FCSTD DOCUMENT  (FreeCAD 0.20R29177 (Git))
Label: Cote10PortraitVesa
License: All rights reserved
LicenseURL: http://en.wikipedia.org/wiki/All_rights_reserved
objects: TechDraw::DrawViewDimension×36, TechDraw::DrawSVGTemplate×2, TechDraw::DrawPage×2, Sketcher::SketchObject×1, PartDesign::Body×1, TechDraw::DrawProjGroupItem×1, TechDraw::DrawProjGroup×1
note: 2 computed .brp shape members not serialized (recipe doc carries the construction recipe); baked Part::Feature solids carry a one-line shape summary decoded from their .brp
EXTERNAL_REF file=DonneesBoitier.FCStd obj=Spreadsheet

FEATURE [Sketcher::SketchObject] Sketch
  FullyConstrained = true
  MapMode = 5
  Support = -> [XY_Plane001]
  expr: Constraints[0] = <<DonneesBoitier>>#<<Spreadsheet>>.xxHauteur - <<DonneesBoitier>>#<<Spreadsheet>>.xxFaEspaceHaut / 2 + <<DonneesBoitier>>#<<Spreadsheet>>.xxHautEncocheFemelle / 2
  expr: Constraints[106] = 10mm
  expr: Constraints[108] = 10mm
  expr: Constraints[109] = 15mm
  expr: Constraints[112] = 15mm
  expr: Constraints[117] = <<DonneesBoitier>>#<<Spreadsheet>>.xxDistEcrou
  expr: Constraints[147] = <<DonneesBoitier>>#<<Spreadsheet>>.xxLongVis
  expr: Constraints[148] = <<DonneesBoitier>>#<<Spreadsheet>>.xxLongVis
  expr: Constraints[151] = <<DonneesBoitier>>#<<Spreadsheet>>.xxEspaceTrouEncoche * 2
  expr: Constraints[158] = <<DonneesBoitier>>#<<Spreadsheet>>.xxEpaisseurEcran - <<DonneesBoitier>>#<<Spreadsheet>>.xxEpEncoche
  expr: Constraints[24] = <<DonneesBoitier>>#<<Spreadsheet>>.xxLongEncoches
  expr: Constraints[262] = <<DonneesBoitier>>#<<Spreadsheet>>.xxDiametreTrou
  expr: Constraints[297] = <<DonneesBoitier>>#<<Spreadsheet>>.xxEspaceTrouEncoche
  expr: Constraints[299] = <<DonneesBoitier>>#<<Spreadsheet>>.xxHauteur - <<DonneesBoitier>>#<<Spreadsheet>>.xxHauteurEncasEcran - <<DonneesBoitier>>#<<Spreadsheet>>.xxFaEspaceHaut * 1.5
  expr: Constraints[36] = <<DonneesBoitier>>#<<Spreadsheet>>.xxLargEconche
  expr: Constraints[59] = <<DonneesBoitier>>#Spreadsheet.xxLargLatHaut
  expr: Constraints[60] = 25mm
  expr: Constraints[61] = <<DonneesBoitier>>#Spreadsheet.xxHauteurEncasEcran / 2 + <<DonneesBoitier>>#Spreadsheet.xxHautEncocheFemelle / 2 + <<DonneesBoitier>>#Spreadsheet.xxFaEspaceHaut / 2
  expr: Constraints[96] = <<DonneesBoitier>>#<<Spreadsheet>>.xxEpEcrou
  sketch-geometry (110):
    g0: LineSegment StartX=0 StartY=0 StartZ=0 EndX=-195.5 EndY=0 EndZ=0
    g1: LineSegment StartX=0 StartY=0 StartZ=0 EndX=6e-16 EndY=10 EndZ=0
    g2: LineSegment StartX=6e-16 StartY=10 StartZ=0 EndX=-8.66025 EndY=15 EndZ=0
    g3: LineSegment StartX=-8.66025 StartY=15 StartZ=0 EndX=-8.66025 EndY=10 EndZ=0
    g4: ArcOfCircle CenterX=0 CenterY=76.1243 CenterZ=0 NormalX=0 NormalY=0 NormalZ=1 AngleXU=0 Radius=66.689 StartAngle=2.73334 EndAngle=4.58216
    g5: LineSegment StartX=-34.7885 StartY=158.361 StartZ=0 EndX=-38.2526 EndY=160.361 EndZ=0
    g6: LineSegment StartX=-42.2526 StartY=153.432 StartZ=0 EndX=-38.7885 EndY=151.432 EndZ=0
    g7: LineSegment StartX=-42.2526 StartY=153.432 StartZ=0 EndX=-41.5651 EndY=154.623 EndZ=0
    g8: LineSegment StartX=-41.5651 StartY=154.623 StartZ=0 EndX=-44.1632 EndY=156.123 EndZ=0
    g9: LineSegment StartX=-44.1632 StartY=156.123 StartZ=0 EndX=-41.5382 EndY=160.67 EndZ=0
    g10: LineSegment StartX=-41.5382 StartY=160.67 StartZ=0 EndX=-38.9401 EndY=159.17 EndZ=0
    g11: LineSegment StartX=-38.9401 StartY=159.17 StartZ=0 EndX=-38.2526 EndY=160.361 EndZ=0
    g12: LineSegment StartX=-83.2859 StartY=186.361 StartZ=0 EndX=-79.8218 EndY=184.361 EndZ=0
    g13: LineSegment StartX=-83.8218 StartY=177.432 StartZ=0 EndX=-87.2859 EndY=179.432 EndZ=0
    g14: LineSegment StartX=-83.8218 StartY=177.432 StartZ=0 EndX=-83.1343 EndY=178.623 EndZ=0
    g15: LineSegment StartX=-83.1343 StartY=178.623 StartZ=0 EndX=-79.6702 EndY=176.623 EndZ=0
    g16: LineSegment StartX=-79.6702 StartY=176.623 StartZ=0 EndX=-77.0452 EndY=181.17 EndZ=0
    g17: LineSegment StartX=-77.0452 StartY=181.17 StartZ=0 EndX=-80.5093 EndY=183.17 EndZ=0
    g18: LineSegment StartX=-80.5093 StartY=183.17 StartZ=0 EndX=-79.8218 EndY=184.361 EndZ=0
    g19: LineSegment StartX=-12.95 StartY=316.186 StartZ=0 EndX=8.70064 EndY=303.686 EndZ=0
    g20: LineSegment StartX=21.691 StartY=296.186 StartZ=0 EndX=43.3417 EndY=283.686 EndZ=0
    g21: LineSegment StartX=8.70064 StartY=303.686 StartZ=0 EndX=6.20064 EndY=299.356 EndZ=0
    g22: LineSegment StartX=6.20064 StartY=299.356 StartZ=0 EndX=19.191 EndY=291.856 EndZ=0
    g23: LineSegment StartX=19.191 StartY=291.856 StartZ=0 EndX=21.691 EndY=296.186 EndZ=0
    g24: LineSegment StartX=-32.4583 StartY=152.396 StartZ=0 EndX=-88.75 EndY=184.896 EndZ=0
    g25: LineSegment StartX=-43.7083 StartY=132.911 StartZ=0 EndX=-100 EndY=165.411 EndZ=0
    g26: LineSegment StartX=43.3417 StartY=283.686 StartZ=0 EndX=-17.4583 EndY=178.377 EndZ=0
    g27: LineSegment StartX=-47.4583 StartY=126.416 StartZ=0 EndX=-61.2083 EndY=102.6 EndZ=0
    g28: LineSegment StartX=-17.4583 StartY=178.377 StartZ=0 EndX=-13.1282 EndY=175.877 EndZ=0
    g29: LineSegment StartX=-13.1282 StartY=175.877 StartZ=0 EndX=-20.6282 EndY=162.887 EndZ=0
    g30: LineSegment StartX=-20.6282 StartY=162.887 StartZ=0 EndX=-24.9583 EndY=165.387 EndZ=0
    g31: LineSegment StartX=-39.9583 StartY=139.406 StartZ=0 EndX=-35.6282 EndY=136.906 EndZ=0
    g32: LineSegment StartX=-35.6282 StartY=136.906 StartZ=0 EndX=-43.1282 EndY=123.916 EndZ=0
    g33: LineSegment StartX=-43.1282 StartY=123.916 StartZ=0 EndX=-47.4583 EndY=126.416 EndZ=0
    g34: LineSegment StartX=-81.25 StartY=197.887 StartZ=0 EndX=-85.5801 EndY=200.387 EndZ=0
    g35: LineSegment StartX=-85.5801 StartY=200.387 StartZ=0 EndX=-78.0801 EndY=213.377 EndZ=0
    g36: LineSegment StartX=-78.0801 StartY=213.377 StartZ=0 EndX=-73.75 EndY=210.877 EndZ=0
    g37: LineSegment StartX=-103.75 StartY=158.916 StartZ=0 EndX=-108.08 EndY=161.416 EndZ=0
    g38: LineSegment StartX=-108.08 StartY=161.416 StartZ=0 EndX=-100.58 EndY=174.406 EndZ=0
    g39: LineSegment StartX=-100.58 StartY=174.406 StartZ=0 EndX=-96.25 EndY=171.906 EndZ=0
    g40: LineSegment StartX=-195.5 StartY=0 StartZ=0 EndX=5.68e-14 EndY=338.616 EndZ=0
    g41: LineSegment StartX=-35.476 StartY=157.17 StartZ=0 EndX=-34.7885 EndY=158.361 EndZ=0
    g42: LineSegment StartX=-38.7885 StartY=151.432 StartZ=0 EndX=-38.101 EndY=152.623 EndZ=0
    g43: LineSegment StartX=-24.9583 StartY=165.387 StartZ=0 EndX=-31.1458 EndY=154.67 EndZ=0
    g44: LineSegment StartX=-33.7708 StartY=150.123 StartZ=0 EndX=-39.9583 EndY=139.406 EndZ=0
    g45: LineSegment StartX=-35.476 StartY=157.17 StartZ=0 EndX=-31.1458 EndY=154.67 EndZ=0
    g46: LineSegment StartX=-38.101 StartY=152.623 StartZ=0 EndX=-33.7708 EndY=150.123 EndZ=0
    g47: LineSegment StartX=-96.25 StartY=171.906 StartZ=0 EndX=-90.0625 EndY=182.623 EndZ=0
    g48: LineSegment StartX=-81.25 StartY=197.887 StartZ=0 EndX=-87.4375 EndY=187.17 EndZ=0
    g49: LineSegment StartX=-83.9734 StartY=185.17 StartZ=0 EndX=-83.2859 EndY=186.361 EndZ=0
    g50: LineSegment StartX=-87.2859 StartY=179.432 StartZ=0 EndX=-86.5984 EndY=180.623 EndZ=0
    g51: LineSegment StartX=-90.0625 StartY=182.623 StartZ=0 EndX=-86.5984 EndY=180.623 EndZ=0
    g52: LineSegment StartX=-87.4375 StartY=187.17 StartZ=0 EndX=-83.9734 EndY=185.17 EndZ=0
    g53: LineSegment StartX=-73.75 StartY=210.877 StartZ=0 EndX=-58.75 EndY=236.858 EndZ=0
    g54: LineSegment StartX=-58.75 StartY=236.858 StartZ=0 EndX=-12.95 EndY=316.186 EndZ=0
    g55: LineSegment StartX=-118.75 StartY=132.935 StartZ=0 EndX=-103.75 EndY=158.916 EndZ=0
    g56: LineSegment StartX=-173.561 StartY=0 StartZ=0 EndX=3.50448 EndY=306.686 EndZ=0
    g57: LineSegment StartX=-12.2955 StartY=279.319 StartZ=0 EndX=-7.96539 EndY=276.819 EndZ=0
    g58: LineSegment StartX=-7.96539 StartY=276.819 StartZ=0 EndX=-15.4654 EndY=263.829 EndZ=0
    g59: LineSegment StartX=-15.4654 StartY=263.829 StartZ=0 EndX=-19.7955 EndY=266.329 EndZ=0
    g60: LineSegment StartX=-19.7955 StartY=266.329 StartZ=0 EndX=-12.2955 EndY=279.319 EndZ=0
    g61: LineSegment StartX=-34.7955 StartY=240.348 StartZ=0 EndX=-30.4654 EndY=237.848 EndZ=0
    g62: LineSegment StartX=-30.4654 StartY=237.848 StartZ=0 EndX=-37.9654 EndY=224.858 EndZ=0
    g63: LineSegment StartX=-42.2955 StartY=227.358 StartZ=0 EndX=-34.7955 EndY=240.348 EndZ=0
    g64: LineSegment StartX=-37.9654 StartY=224.858 StartZ=0 EndX=-42.2955 EndY=227.358 EndZ=0
    g65: LineSegment StartX=-57.2955 StartY=201.377 StartZ=0 EndX=-52.9654 EndY=198.877 EndZ=0
    g66: LineSegment StartX=-52.9654 StartY=198.877 StartZ=0 EndX=-60.4654 EndY=185.887 EndZ=0
    g67: LineSegment StartX=-64.7955 StartY=188.387 StartZ=0 EndX=-57.2955 EndY=201.377 EndZ=0
    g68: LineSegment StartX=-60.4654 StartY=185.887 StartZ=0 EndX=-64.7955 EndY=188.387 EndZ=0
    g69: LineSegment StartX=-85.5801 StartY=200.387 StartZ=0 EndX=-60.4654 EndY=185.887 EndZ=0
    g70: LineSegment StartX=-132.296 StartY=71.4734 StartZ=0 EndX=-127.965 EndY=68.9734 EndZ=0
    g71: LineSegment StartX=-127.965 StartY=68.9734 StartZ=0 EndX=-120.465 EndY=81.9638 EndZ=0
    g72: LineSegment StartX=-120.465 StartY=81.9638 StartZ=0 EndX=-124.796 EndY=84.4638 EndZ=0
    g73: LineSegment StartX=-124.796 StartY=84.4638 StartZ=0 EndX=-132.296 EndY=71.4734 EndZ=0
    g74: LineSegment StartX=-109.796 StartY=110.445 StartZ=0 EndX=-105.465 EndY=107.945 EndZ=0
    g75: LineSegment StartX=-105.465 StartY=107.945 StartZ=0 EndX=-97.9654 EndY=120.935 EndZ=0
    g76: LineSegment StartX=-102.296 StartY=123.435 StartZ=0 EndX=-109.796 EndY=110.445 EndZ=0
    g77: LineSegment StartX=-97.9654 StartY=120.935 StartZ=0 EndX=-102.296 EndY=123.435 EndZ=0
    g78: LineSegment StartX=-87.2955 StartY=149.416 StartZ=0 EndX=-82.9654 EndY=146.916 EndZ=0
    g79: LineSegment StartX=-82.9654 StartY=146.916 StartZ=0 EndX=-75.4654 EndY=159.906 EndZ=0
    g80: LineSegment StartX=-79.7955 StartY=162.406 StartZ=0 EndX=-87.2955 EndY=149.416 EndZ=0
    g81: LineSegment StartX=-75.4654 StartY=159.906 StartZ=0 EndX=-79.7955 EndY=162.406 EndZ=0
    g82: LineSegment StartX=-195.5 StartY=0 StartZ=0 EndX=-178.25 EndY=29.8779 EndZ=0
    g83: LineSegment StartX=-170.75 StartY=42.8683 StartZ=0 EndX=-164.563 EndY=53.5853 EndZ=0
    g84: LineSegment StartX=-161.938 StartY=58.132 StartZ=0 EndX=-155.75 EndY=68.849 EndZ=0
    g85: LineSegment StartX=-148.25 StartY=81.8394 StartZ=0 EndX=-118.75 EndY=132.935 EndZ=0
    g86: LineSegment StartX=-148.25 StartY=81.8394 StartZ=0 EndX=-152.58 EndY=84.3394 EndZ=0
    g87: LineSegment StartX=-152.58 StartY=84.3394 StartZ=0 EndX=-160.08 EndY=71.349 EndZ=0
    g88: LineSegment StartX=-160.08 StartY=71.349 StartZ=0 EndX=-155.75 EndY=68.849 EndZ=0
    g89: LineSegment StartX=-170.75 StartY=42.8683 StartZ=0 EndX=-175.08 EndY=45.3683 EndZ=0
    g90: LineSegment StartX=-175.08 StartY=45.3683 StartZ=0 EndX=-182.58 EndY=32.3779 EndZ=0
    g91: LineSegment StartX=-182.58 StartY=32.3779 StartZ=0 EndX=-178.25 EndY=29.8779 EndZ=0
    g92: LineSegment StartX=-164.563 StartY=53.5853 StartZ=0 EndX=-161.098 EndY=51.5853 EndZ=0
    g93: LineSegment StartX=-161.098 StartY=51.5853 StartZ=0 EndX=-161.786 EndY=50.3945 EndZ=0
    g94: LineSegment StartX=-161.786 StartY=50.3945 StartZ=0 EndX=-158.322 EndY=48.3945 EndZ=0
    g95: LineSegment StartX=-158.322 StartY=48.3945 StartZ=0 EndX=-157.634 EndY=49.5853 EndZ=0
    g96: LineSegment StartX=-157.634 StartY=49.5853 StartZ=0 EndX=-154.17 EndY=47.5853 EndZ=0
    g97: LineSegment StartX=-154.17 StartY=47.5853 StartZ=0 EndX=-151.545 EndY=52.132 EndZ=0
    g98: LineSegment StartX=-151.545 StartY=52.132 StartZ=0 EndX=-155.009 EndY=54.132 EndZ=0
    g99: LineSegment StartX=-155.009 StartY=54.132 StartZ=0 EndX=-154.322 EndY=55.3227 EndZ=0
    g100: LineSegment StartX=-154.322 StartY=55.3227 StartZ=0 EndX=-157.786 EndY=57.3227 EndZ=0
    g101: LineSegment StartX=-157.786 StartY=57.3227 StartZ=0 EndX=-158.473 EndY=56.132 EndZ=0
    g102: LineSegment StartX=-158.473 StartY=56.132 StartZ=0 EndX=-161.938 EndY=58.132 EndZ=0
    g103: GeomPoint X=-163.25 Y=55.8586 Z=0
    g104: LineSegment StartX=-195.5 StartY=0 StartZ=0 EndX=-162.591 EndY=19 EndZ=0
    g105: ArcOfCircle CenterX=-178.179 CenterY=10 CenterZ=0 NormalX=0 NormalY=0 NormalZ=1 AngleXU=0 Radius=10 StartAngle=2.61799 EndAngle=4.71239
    g106: LineSegment StartX=-12.95 StartY=316.186 StartZ=0 EndX=-5.99552 EndY=290.231 EndZ=0
    g107: LineSegment StartX=43.3417 StartY=283.686 StartZ=0 EndX=-19.4955 EndY=266.849 EndZ=0
    g108: ArcOfCircle CenterX=-7.77362 CenterY=296.867 CenterZ=0 NormalX=0 NormalY=0 NormalZ=1 AngleXU=0 Radius=14.1421 StartAngle=1.0472 EndAngle=2.61799
    g109: ArcOfCircle CenterX=24.0231 CenterY=278.509 CenterZ=0 NormalX=0 NormalY=0 NormalZ=1 AngleXU=0 Radius=14.1421 StartAngle=5.75959 EndAngle=7.33038
  constraints (322):
    c: Distance(g0,g19) = 365.1
    c: Tangent(g19,g20)
    c: Parallel(g26,g29)
    c: Parallel(g29,g35)
    c: Parallel(g32,g38)
    c: Parallel(g21,g23)
    c: Coincident(g19,g54)
    c: Coincident(g21,g19)
    c: Coincident(g23,g20)
    c: Coincident(g20,g26)
    c: Coincident(g53,g36)
    c: Coincident(g35,g34)
    c: Coincident(g26,g28)
    c: Coincident(g29,g28)
    c: Coincident(g29,g30)
    c: Coincident(g30,g43)
    c: Parallel(g36,g19)
    c: Parallel(g34,g19)
    c: Parallel(g28,g30)
    c: Parallel(g30,g20)
    c: Parallel(g37,g39)
    c: Parallel(g39,g31)
    c: Parallel(g31,g33)
    c: Parallel(g33,g20)
    c: Distance(g26,g28) = 5
    c: Equal(g28,g36)
    c: Equal(g36,g34)
    c: Equal(g34,g30)
    c: Equal(g30,g23)
    c: Equal(g23,g21)
    c: Equal(g30,g31)
    c: Equal(g31,g33)
    c: Equal(g33,g37)
    c: Equal(g37,g39)
    c: Coincident(g22,g21)
    c: Coincident(g22,g23)
    c: Distance(g21,g22) = 15
    c: Equal(g22,g35)
    c: Equal(g35,g29)
    c: Equal(g29,g32)
    c: Equal(g32,g38)
    c: Coincident(g35,g36)
    c: PointOnObject(g0,g-1)
    c: Coincident(g55,g37)
    c: Coincident(g38,g39)
    c: Coincident(g37,g38)
    c: Coincident(g40,g0)
    c: PointOnObject(g40,g-2)
    c: Angle(g0,g40) = 1.0472
    c: Distance(g0,g40) = 391
    c: Coincident(g0,g1)
    c: Coincident(g0,g-1)
    c: Symmetric(g39,g55,g25)
    c: Coincident(g44,g31)
    c: Coincident(g32,g31)
    c: Coincident(g32,g33)
    c: Coincident(g27,g33)
    c: Symmetric(g27,g44,g25)
    c: Coincident(g27,g4)
    c: Distance(g19,g20) = 65
    c: Distance(g19,g19) = 25
    c: Distance(g20,g24) = 151.6
    c: Symmetric(g8,g9,g24)
    c: Symmetric(g15,g16,g24)
    c: Coincident(g41,g5)
    c: Coincident(g10,g9)
    c: Coincident(g9,g8)
    c: Coincident(g42,g6)
    c: Parallel(g8,g10)
    c: Parallel(g10,g24)
    c: Coincident(g11,g10)
    c: Parallel(g11,g7)
    c: Parallel(g7,g9)
    c: Coincident(g5,g11)
    c: Parallel(g5,g6)
    c: Parallel(g6,g24)
    c: Coincident(g6,g7)
    c: Coincident(g8,g7)
    c: Distance(g5,g41) = 4
    c: Equal(g5,g6)
    c: Distance(g42,g41) = 8
    c: Symmetric(g41,g42,g24)
    c: Distance(g8,g9) = 5.25
    c: Symmetric(g39,g34,g24)
    c: Coincident(g16,g17)
    c: Coincident(g15,g16)
    c: Coincident(g13,g50)
    c: Coincident(g12,g49)
    c: Symmetric(g14,g17,g24)
    c: Symmetric(g12,g13,g24)
    c: Parallel(g24,g17)
    c: Parallel(g17,g12)
    c: Coincident(g18,g12)
    c: Coincident(g18,g17)
    c: Coincident(g15,g14)
    c: Coincident(g14,g13)
    c: Distance(g49,g12) = 4
    c: Distance(g50,g49) = 8
    c: Distance(g15,g16) = 5.25
    c: Parallel(g13,g24)
    c: PointOnObject(g24,g40)
    c: PointOnObject(g4,g-2)
    c: Coincident(g4,g3)
    c: Coincident(g1,g2)
    c: Coincident(g2,g3)
    c: Distance(g2,g3) = 5
    c: Distance(g2,g1) = 10
    c: Angle(g-1,g1) = 1.5708
    c: Distance(g0,g1) = 10
    c: Distance(g2,g0) = 15
    c: Distance(g4,g27) = 27.5
    c: Parallel(g3,g1)
    c: Distance(g43,g24) = 15
    c: Parallel(g38,g41)
    c: Parallel(g38,g42)
    c: Equal(g7,g42)
    c: Parallel(g43,g32)
    c: Distance(g41,g43) = 5
    c: Coincident(g45,g41)
    c: Coincident(g45,g43)
    c: Parallel(g24,g45)
    c: Coincident(g46,g42)
    c: Coincident(g46,g44)
    c: Parallel(g46,g24)
    c: Equal(g46,g45)
    c: Symmetric(g42,g41,g24)
    c: Parallel(g25,g24)
    c: Equal(g25,g24)
    c: Coincident(g47,g39)
    c: PointOnObject(g47,g40)
    c: Coincident(g48,g34)
    c: PointOnObject(g48,g40)
    c: Symmetric(g47,g48,g24)
    c: Parallel(g49,g21)
    c: Parallel(g50,g21)
    c: Parallel(g50,g14)
    c: Equal(g50,g14)
    c: Equal(g18,g49)
    c: Parallel(g49,g18)
    c: PointOnObject(g52,g40)
    c: Coincident(g52,g49)
    c: Parallel(g51,g13)
    c: Parallel(g13,g52)
    c: Equal(g52,g51)
    c: Equal(g51,g12)
    c: Coincident(g51,g47)
    c: Coincident(g51,g50)
    c: Distance(g47,g15) = 12
    c: Distance(g8,g44) = 12
    c: Parallel(g53,g26)
    c: Parallel(g54,g26)
    c: Distance(g36,g53) = 30
    c: PointOnObject(g54,g40)
    c: Parallel(g37,g25)
    c: Symmetric(g31,g30,g24)
    c: Parallel(g27,g55)
    c: PointOnObject(g56,g0)
    c: PointOnObject(g56,g19)
    c: Distance(g56,g19) = 19
    c: PointOnObject(g57,g56)
    c: Coincident(g57,g58)
    c: Coincident(g58,g59)
    c: PointOnObject(g59,g56)
    c: Coincident(g59,g60)
    c: Coincident(g60,g57)
    c: Equal(g36,g59)
    c: Equal(g59,g57)
    c: Parallel(g59,g57)
    c: Parallel(g57,g19)
    c: Equal(g58,g35)
    c: Coincident(g61,g62)
    c: Coincident(g62,g64)
    c: Coincident(g64,g63)
    c: Coincident(g63,g61)
    c: Equal(g64,g61)
    c: Parallel(g64,g61)
    c: PointOnObject(g63,g56)
    c: PointOnObject(g61,g56)
    c: Equal(g36,g64)
    c: Parallel(g36,g64)
    c: Equal(g35,g62)
    c: Coincident(g65,g66)
    c: Coincident(g66,g68)
    c: Coincident(g68,g67)
    c: Equal(g68,g65)
    c: Parallel(g68,g65)
    c: PointOnObject(g67,g56)
    c: PointOnObject(g65,g56)
    c: Equal(g35,g67)
    c: Coincident(g67,g65)
    c: Parallel(g36,g65)
    c: Equal(g68,g36)
    c: Distance(g65,g63) = 30
    c: Distance(g61,g59) = 30
    c: Coincident(g69,g34)
    c: Parallel(g69,g24)
    c: Coincident(g66,g69)
    c: Coincident(g70,g71)
    c: Coincident(g71,g72)
    c: Coincident(g72,g73)
    c: Coincident(g73,g70)
    c: Equal(g72,g70)
    c: Parallel(g72,g70)
    c: Coincident(g74,g75)
    c: Coincident(g75,g77)
    c: Coincident(g77,g76)
    c: Coincident(g76,g74)
    c: Equal(g77,g74)
    c: Parallel(g77,g74)
    c: Coincident(g78,g79)
    c: Coincident(g79,g81)
    c: Coincident(g81,g80)
    c: Equal(g81,g78)
    c: Parallel(g81,g78)
    c: Coincident(g80,g78)
    c: Distance(g78,g76) = 30
    c: Distance(g74,g72) = 30
    c: Parallel(g38,g80)
    c: Parallel(g79,g75)
    c: Parallel(g76,g71)
    c: Parallel(g39,g81)
    c: Parallel(g78,g77)
    c: Parallel(g74,g72)
    c: Equal(g78,g77)
    c: Equal(g74,g37)
    c: Equal(g79,g38)
    c: Equal(g38,g75)
    c: Equal(g75,g71)
    c: PointOnObject(g72,g56)
    c: Symmetric(g80,g67,g24)
    c: Equal(g72,g74)
    c: PointOnObject(g76,g56)
    c: Distance(g55,g37) = 30
    c: Coincident(g54,g53)
    c: Coincident(g82,g0)
    c: PointOnObject(g82,g40)
    c: PointOnObject(g83,g40)
    c: PointOnObject(g83,g40)
    c: PointOnObject(g84,g40)
    c: PointOnObject(g85,g40)
    c: Coincident(g85,g55)
    c: Parallel(g55,g56)
    c: Parallel(g85,g56)
    c: PointOnObject(g37,g40)
    c: Coincident(g85,g86)
    c: Coincident(g86,g87)
    c: Coincident(g87,g88)
    c: Coincident(g88,g84)
    c: Coincident(g83,g89)
    c: Coincident(g89,g90)
    c: Coincident(g90,g91)
    c: Coincident(g91,g82)
    c: Parallel(g90,g87)
    c: Parallel(g87,g40)
    c: Equal(g90,g87)
    c: Equal(g87,g38)
    c: Parallel(g91,g89)
    c: Parallel(g89,g88)
    c: Parallel(g88,g86)
    c: Parallel(g86,g37)
    c: Equal(g86,g37)
    c: Equal(g89,g88)
    c: Distance(g83,g84) = 5.25
    c: Coincident(g92,g93)
    c: Coincident(g93,g94)
    c: Coincident(g94,g95)
    c: Coincident(g95,g96)
    c: Coincident(g96,g97)
    c: Coincident(g97,g98)
    c: Coincident(g98,g99)
    c: Coincident(g99,g100)
    c: Coincident(g100,g101)
    c: Coincident(g101,g102)
    c: Coincident(g102,g84)
    c: Parallel(g92,g102)
    c: Parallel(g102,g100)
    c: Parallel(g100,g94)
    c: Parallel(g94,g96)
    c: Parallel(g96,g98)
    c: Parallel(g98,g88)
    c: Parallel(g93,g101)
    c: Parallel(g101,g99)
    c: Parallel(g99,g95)
    c: Parallel(g95,g97)
    c: Parallel(g97,g56)
    c: Equal(g92,g102)
    c: Equal(g102,g51)
    c: Equal(g94,g100)
    c: Equal(g100,g13)
    c: Equal(g15,g98)
    c: Equal(g98,g96)
    c: Equal(g93,g95)
    c: Equal(g95,g99)
    c: Equal(g99,g101)
    c: Equal(g101,g14)
    c: Equal(g16,g97)
    c: Symmetric(g83,g84,g103)
    c: Distance(g83,g103) = 15
    c: Symmetric(g83,g84,g103)
    c: Distance(g0,g103) = 64.5
    c: Coincident(g104,g0)
    c: PointOnObject(g104,g56)
    c: Angle(g0,g104) = 0.523599
    c: PointOnObject(g105,g104)
    c: Distance(g0,g105) = 20
    c: PointOnObject(g105,g0)
    c: Tangent(g105,g82) = 1.5708
    c: PointOnObject(g106,g56)
    c: Coincident(g107,g20)
    c: PointOnObject(g107,g56)
    c: Angle(g106,g19) = 0.785398
    c: Coincident(g106,g19)
    c: Angle(g20,g107) = 0.785398
    c: PointOnObject(g108,g106)
    c: Distance(g19,g108) = 20
    c: PointOnObject(g108,g54)
    c: Tangent(g108,g54,g108) = 1.5708
    c: PointOnObject(g108,g19)
    c: PointOnObject(g109,g107)
    c: Distance(g109,g20) = 20
    c: Tangent(g109,g20) = 1.5708
    c: PointOnObject(g109,g26)
FEATURE [PartDesign::Body] Body001
  Group = -> [Sketch]
  Origin = -> Origin001
FEATURE [TechDraw::DrawSVGTemplate] Template
  Height = 297
  Orientation = 0
  Width = 210
FEATURE [TechDraw::DrawProjGroupItem] ProjItem  label="Front"
  CoarseView = false
  Direction = (0,0,1)
  Focus = 100
  HardHidden = false
  IsoCount = 0
  IsoHidden = false
  IsoVisible = false
  LockPosition = true
  Perspective = false
  Rotation = 0
  RotationVector = (1,0,0)
  Scale = 0.6
  ScaleType = 2
  SeamHidden = false
  SeamVisible = true
  SmoothHidden = false
  SmoothVisible = true
  Source = -> [Sketch]
  Type = 0
  X = 0
  XDirection = (1,0,0)
  Y = 0
FEATURE [TechDraw::DrawProjGroup] ProjGroup
  Anchor = -> ProjItem
  AutoDistribute = true
  LockPosition = false
  ProjectionType = 0
  Rotation = 0
  Scale = 0.6
  ScaleType = 2
  Source = -> [Sketch]
  Views = -> [ProjItem]
  X = 107.785
  Y = 166.014
  spacingX = 15
  spacingY = 15
FEATURE [TechDraw::DrawViewDimension] Dimension
  AngleOverride = false
  Arbitrary = false
  ArbitraryTolerances = false
  EqualTolerance = true
  ExtensionAngle = 0
  FormatSpec = %.2w
  FormatSpecOverTolerance = %+.2w
  FormatSpecUnderTolerance = %+.2w
  Inverted = false
  LineAngle = 0
  LockPosition = false
  MeasureType = 1
  OverTolerance = 0
  References2D = -> [ProjItem]
  Rotation = 0
  ScaleType = 0
  TheoreticalExact = false
  Type = 0
  UnderTolerance = 0
  X = -60.3975
  Y = 20.9164
FEATURE [TechDraw::DrawViewDimension] Dimension001
  AngleOverride = false
  Arbitrary = false
  ArbitraryTolerances = false
  EqualTolerance = true
  ExtensionAngle = 0
  FormatSpec = %.2w
  FormatSpecOverTolerance = %+.2w
  FormatSpecUnderTolerance = %+.2w
  Inverted = false
  LineAngle = 0
  LockPosition = false
  MeasureType = 1
  OverTolerance = 0
  References2D = -> [ProjItem]
  Rotation = 0
  ScaleType = 0
  TheoreticalExact = false
  Type = 0
  UnderTolerance = 0
  X = 66.5364
  Y = 110.062
FEATURE [TechDraw::DrawViewDimension] Dimension002
  AngleOverride = false
  Arbitrary = false
  ArbitraryTolerances = false
  EqualTolerance = true
  ExtensionAngle = 0
  FormatSpec = %.2w
  FormatSpecOverTolerance = %+.2w
  FormatSpecUnderTolerance = %+.2w
  Inverted = false
  LineAngle = 0
  LockPosition = false
  MeasureType = 1
  OverTolerance = 0
  References2D = -> [ProjItem]
  Rotation = 0
  ScaleType = 0
  TheoreticalExact = false
  Type = 0
  UnderTolerance = 0
  X = -11.9713
  Y = -105.246
FEATURE [TechDraw::DrawViewDimension] Dimension003
  AngleOverride = false
  Arbitrary = false
  ArbitraryTolerances = false
  EqualTolerance = true
  ExtensionAngle = 0
  FormatSpec = %.2w
  FormatSpecOverTolerance = %+.2w
  FormatSpecUnderTolerance = %+.2w
  Inverted = false
  LineAngle = 0
  LockPosition = false
  MeasureType = 1
  OverTolerance = 0
  References2D = -> [ProjItem]
  Rotation = 0
  ScaleType = 0
  TheoreticalExact = false
  Type = 0
  UnderTolerance = 0
  X = -76.7896
  Y = -76.6895
FEATURE [TechDraw::DrawViewDimension] Dimension004
  AngleOverride = false
  Arbitrary = false
  ArbitraryTolerances = false
  EqualTolerance = true
  ExtensionAngle = 0
  FormatSpec = %.2w
  FormatSpecOverTolerance = %+.2w
  FormatSpecUnderTolerance = %+.2w
  Inverted = false
  LineAngle = 0
  LockPosition = false
  MeasureType = 1
  OverTolerance = 0
  References2D = -> [ProjItem]
  Rotation = 0
  ScaleType = 0
  TheoreticalExact = false
  Type = 0
  UnderTolerance = 0
  X = -54.0758
  Y = -84.7026
FEATURE [TechDraw::DrawViewDimension] Dimension005
  AngleOverride = false
  Arbitrary = false
  ArbitraryTolerances = false
  EqualTolerance = true
  ExtensionAngle = 0
  FormatSpec = %.2w
  FormatSpecOverTolerance = %+.2w
  FormatSpecUnderTolerance = %+.2w
  Inverted = false
  LineAngle = 0
  LockPosition = false
  MeasureType = 0
  OverTolerance = 0
  References2D = -> [ProjItem]
  References3D = -> [Body001]
  Rotation = 0
  ScaleType = 0
  TheoreticalExact = false
  Type = 0
  UnderTolerance = 0
  X = -86.9192
  Y = -64.0042
FEATURE [TechDraw::DrawViewDimension] Dimension006
  AngleOverride = false
  Arbitrary = false
  ArbitraryTolerances = false
  EqualTolerance = true
  ExtensionAngle = 0
  FormatSpec = %.2w
  FormatSpecOverTolerance = %+.2w
  FormatSpecUnderTolerance = %+.2w
  Inverted = false
  LineAngle = 0
  LockPosition = false
  MeasureType = 1
  OverTolerance = 0
  References2D = -> [ProjItem]
  Rotation = 0
  ScaleType = 0
  TheoreticalExact = false
  Type = 0
  UnderTolerance = 0
  X = -72.8236
  Y = -24.3687
FEATURE [TechDraw::DrawViewDimension] Dimension008
  AngleOverride = false
  Arbitrary = false
  ArbitraryTolerances = false
  EqualTolerance = true
  ExtensionAngle = 0
  FormatSpec = %.2w
  FormatSpecOverTolerance = %+.2w
  FormatSpecUnderTolerance = %+.2w
  Inverted = false
  LineAngle = 0
  LockPosition = false
  MeasureType = 1
  OverTolerance = 0
  References2D = -> [ProjItem]
  Rotation = 0
  ScaleType = 0
  TheoreticalExact = false
  Type = 0
  UnderTolerance = 0
  X = -51.5554
  Y = -37.9317
FEATURE [TechDraw::DrawViewDimension] Dimension009
  AngleOverride = false
  Arbitrary = false
  ArbitraryTolerances = false
  EqualTolerance = true
  ExtensionAngle = 0
  FormatSpec = %.2w
  FormatSpecOverTolerance = %+.2w
  FormatSpecUnderTolerance = %+.2w
  Inverted = false
  LineAngle = 0
  LockPosition = false
  MeasureType = 1
  OverTolerance = 0
  References2D = -> [ProjItem]
  Rotation = 0
  ScaleType = 0
  TheoreticalExact = false
  Type = 0
  UnderTolerance = 0
  X = 70.5887
  Y = 99.0628
FEATURE [TechDraw::DrawViewDimension] Dimension010
  AngleOverride = false
  Arbitrary = false
  ArbitraryTolerances = false
  EqualTolerance = true
  ExtensionAngle = 0
  FormatSpec = %.2w
  FormatSpecOverTolerance = %+.2w
  FormatSpecUnderTolerance = %+.2w
  Inverted = false
  LineAngle = 0
  LockPosition = false
  MeasureType = 1
  OverTolerance = 0
  References2D = -> [ProjItem]
  Rotation = 0
  ScaleType = 0
  TheoreticalExact = false
  Type = 0
  UnderTolerance = 0
  X = 32.6057
  Y = 112.891
FEATURE [TechDraw::DrawViewDimension] Dimension011
  AngleOverride = false
  Arbitrary = false
  ArbitraryTolerances = false
  EqualTolerance = true
  ExtensionAngle = 0
  FormatSpec = %.2w
  FormatSpecOverTolerance = %+.2w
  FormatSpecUnderTolerance = %+.2w
  Inverted = false
  LineAngle = 0
  LockPosition = false
  MeasureType = 1
  OverTolerance = 0
  References2D = -> [ProjItem]
  Rotation = 0
  ScaleType = 0
  TheoreticalExact = false
  Type = 0
  UnderTolerance = 0
  X = 59.3802
  Y = 42.5334
FEATURE [TechDraw::DrawViewDimension] Dimension012
  AngleOverride = false
  Arbitrary = false
  ArbitraryTolerances = false
  EqualTolerance = true
  ExtensionAngle = 0
  FormatSpec = %.2w
  FormatSpecOverTolerance = %+.2w
  FormatSpecUnderTolerance = %+.2w
  Inverted = false
  LineAngle = 0
  LockPosition = false
  MeasureType = 1
  OverTolerance = 0
  References2D = -> [ProjItem]
  Rotation = 0
  ScaleType = 0
  TheoreticalExact = false
  Type = 0
  UnderTolerance = 0
  X = 47.4559
  Y = 3.80308
FEATURE [TechDraw::DrawViewDimension] Dimension013
  AngleOverride = false
  Arbitrary = false
  ArbitraryTolerances = false
  EqualTolerance = true
  ExtensionAngle = 0
  FormatSpec = %.2w
  FormatSpecOverTolerance = %+.2w
  FormatSpecUnderTolerance = %+.2w
  Inverted = false
  LineAngle = 0
  LockPosition = false
  MeasureType = 0
  OverTolerance = 0
  References2D = -> [ProjItem]
  References3D = -> [Body001]
  Rotation = 0
  ScaleType = 0
  TheoreticalExact = false
  Type = 0
  UnderTolerance = 0
  X = 64.8709
  Y = -2.05781
FEATURE [TechDraw::DrawViewDimension] Dimension014
  AngleOverride = false
  Arbitrary = false
  ArbitraryTolerances = false
  EqualTolerance = true
  ExtensionAngle = 0
  FormatSpec = %.2w
  FormatSpecOverTolerance = %+.2w
  FormatSpecUnderTolerance = %+.2w
  Inverted = false
  LineAngle = 0
  LockPosition = false
  MeasureType = 1
  OverTolerance = 0
  References2D = -> [ProjItem]
  Rotation = 0
  ScaleType = 0
  TheoreticalExact = false
  Type = 0
  UnderTolerance = 0
  X = 38.4479
  Y = -33.3461
FEATURE [TechDraw::DrawViewDimension] Dimension015
  AngleOverride = false
  Arbitrary = false
  ArbitraryTolerances = false
  EqualTolerance = true
  ExtensionAngle = 0
  FormatSpec = %.2w
  FormatSpecOverTolerance = %+.2w
  FormatSpecUnderTolerance = %+.2w
  Inverted = false
  LineAngle = 0
  LockPosition = false
  MeasureType = 1
  OverTolerance = 0
  References2D = -> [ProjItem]
  Rotation = 0
  ScaleType = 0
  TheoreticalExact = false
  Type = 0
  UnderTolerance = 0
  X = 0.536424
  Y = 52.781
FEATURE [TechDraw::DrawViewDimension] Dimension016
  AngleOverride = false
  Arbitrary = false
  ArbitraryTolerances = false
  EqualTolerance = true
  ExtensionAngle = 0
  FormatSpec = %.2w
  FormatSpecOverTolerance = %+.2w
  FormatSpecUnderTolerance = %+.2w
  Inverted = false
  LineAngle = 0
  LockPosition = false
  MeasureType = 1
  OverTolerance = 0
  References2D = -> [ProjItem]
  Rotation = 0
  ScaleType = 0
  TheoreticalExact = false
  Type = 0
  UnderTolerance = 0
  X = 40.1506
  Y = 48.1003
FEATURE [TechDraw::DrawViewDimension] Dimension017
  AngleOverride = false
  Arbitrary = false
  ArbitraryTolerances = false
  EqualTolerance = true
  ExtensionAngle = 0
  FormatSpec = %.2w
  FormatSpecOverTolerance = %+.2w
  FormatSpecUnderTolerance = %+.2w
  Inverted = false
  LineAngle = 0
  LockPosition = false
  MeasureType = 1
  OverTolerance = 0
  References2D = -> [ProjItem]
  Rotation = 0
  ScaleType = 0
  TheoreticalExact = false
  Type = 0
  UnderTolerance = 0
  X = 22.546
  Y = 64.0216
FEATURE [TechDraw::DrawViewDimension] Dimension018
  AngleOverride = false
  Arbitrary = false
  ArbitraryTolerances = false
  EqualTolerance = true
  ExtensionAngle = 0
  FormatSpec = %.2w
  FormatSpecOverTolerance = %+.2w
  FormatSpecUnderTolerance = %+.2w
  Inverted = false
  LineAngle = 0
  LockPosition = false
  MeasureType = 1
  OverTolerance = 0
  References2D = -> [ProjItem]
  Rotation = 0
  ScaleType = 0
  TheoreticalExact = false
  Type = 0
  UnderTolerance = 0
  X = 3.19854
  Y = 71.6263
FEATURE [TechDraw::DrawViewDimension] Dimension019
  AngleOverride = false
  Arbitrary = false
  ArbitraryTolerances = false
  EqualTolerance = true
  ExtensionAngle = 0
  FormatSpec = %.2w
  FormatSpecOverTolerance = %+.2w
  FormatSpecUnderTolerance = %+.2w
  Inverted = false
  LineAngle = 0
  LockPosition = false
  MeasureType = 1
  OverTolerance = 0
  References2D = -> [ProjItem]
  Rotation = 0
  ScaleType = 0
  TheoreticalExact = false
  Type = 0
  UnderTolerance = 0
  X = -17.8176
  Y = 55.29
FEATURE [TechDraw::DrawViewDimension] Dimension020
  AngleOverride = false
  Arbitrary = false
  ArbitraryTolerances = false
  EqualTolerance = true
  ExtensionAngle = 0
  FormatSpec = %.2w
  FormatSpecOverTolerance = %+.2w
  FormatSpecUnderTolerance = %+.2w
  Inverted = false
  LineAngle = 0
  LockPosition = false
  MeasureType = 1
  OverTolerance = 0
  References2D = -> [ProjItem]
  Rotation = 0
  ScaleType = 0
  TheoreticalExact = false
  Type = 0
  UnderTolerance = 0
  X = -32.0223
  Y = 30.9678
FEATURE [TechDraw::DrawViewDimension] Dimension021
  AngleOverride = false
  Arbitrary = false
  ArbitraryTolerances = false
  EqualTolerance = true
  ExtensionAngle = 0
  FormatSpec = %.2w
  FormatSpecOverTolerance = %+.2w
  FormatSpecUnderTolerance = %+.2w
  Inverted = false
  LineAngle = 0
  LockPosition = false
  MeasureType = 1
  OverTolerance = 0
  References2D = -> [ProjItem]
  Rotation = 0
  ScaleType = 0
  TheoreticalExact = false
  Type = 0
  UnderTolerance = 0
  X = -43.6432
  Y = 10.1688
FEATURE [TechDraw::DrawViewDimension] Dimension022
  AngleOverride = false
  Arbitrary = false
  ArbitraryTolerances = false
  EqualTolerance = true
  ExtensionAngle = 0
  FormatSpec = %.2w
  FormatSpecOverTolerance = %+.2w
  FormatSpecUnderTolerance = %+.2w
  Inverted = false
  LineAngle = 0
  LockPosition = false
  MeasureType = 1
  OverTolerance = 0
  References2D = -> [ProjItem]
  Rotation = 0
  ScaleType = 0
  TheoreticalExact = false
  Type = 0
  UnderTolerance = 0
  X = -17.669
  Y = -38.0139
FEATURE [TechDraw::DrawViewDimension] Dimension023
  AngleOverride = false
  Arbitrary = false
  ArbitraryTolerances = false
  EqualTolerance = true
  ExtensionAngle = 0
  FormatSpec = %.2w
  FormatSpecOverTolerance = %+.2w
  FormatSpecUnderTolerance = %+.2w
  Inverted = false
  LineAngle = 0
  LockPosition = false
  MeasureType = 1
  OverTolerance = 0
  References2D = -> [ProjItem]
  Rotation = 0
  ScaleType = 0
  TheoreticalExact = false
  Type = 0
  UnderTolerance = 0
  X = 39.8839
  Y = 82.9021
FEATURE [TechDraw::DrawViewDimension] Dimension024
  AngleOverride = false
  Arbitrary = false
  ArbitraryTolerances = false
  EqualTolerance = true
  ExtensionAngle = 0
  FormatSpec = %.2w
  FormatSpecOverTolerance = %+.2w
  FormatSpecUnderTolerance = %+.2w
  Inverted = false
  LineAngle = 0
  LockPosition = false
  MeasureType = 1
  OverTolerance = 0
  References2D = -> [ProjItem]
  Rotation = 0
  ScaleType = 0
  TheoreticalExact = false
  Type = 0
  UnderTolerance = 0
  X = 53.152
  Y = -81.4224
FEATURE [TechDraw::DrawViewDimension] Dimension025
  AngleOverride = false
  Arbitrary = false
  ArbitraryTolerances = false
  EqualTolerance = true
  ExtensionAngle = 0
  FormatSpec = %.2w
  FormatSpecOverTolerance = %+.2w
  FormatSpecUnderTolerance = %+.2w
  Inverted = false
  LineAngle = 0
  LockPosition = false
  MeasureType = 0
  OverTolerance = 0
  References2D = -> [ProjItem]
  References3D = -> [Body001]
  Rotation = 0
  ScaleType = 0
  TheoreticalExact = false
  Type = 0
  UnderTolerance = 0
  X = -52.7731
  Y = -16.3674
FEATURE [TechDraw::DrawViewDimension] Dimension026
  AngleOverride = false
  Arbitrary = false
  ArbitraryTolerances = false
  EqualTolerance = true
  ExtensionAngle = 0
  FormatSpec = %.2w
  FormatSpecOverTolerance = %+.2w
  FormatSpecUnderTolerance = %+.2w
  Inverted = false
  LineAngle = 0
  LockPosition = false
  MeasureType = 1
  OverTolerance = 0
  References2D = -> [ProjItem]
  Rotation = 0
  ScaleType = 0
  TheoreticalExact = false
  Type = 0
  UnderTolerance = 0
  X = 20.9395
  Y = -27.0333
FEATURE [TechDraw::DrawViewDimension] Dimension027
  AngleOverride = false
  Arbitrary = false
  ArbitraryTolerances = false
  EqualTolerance = true
  ExtensionAngle = 0
  FormatSpec = %.2w
  FormatSpecOverTolerance = %+.2w
  FormatSpecUnderTolerance = %+.2w
  Inverted = false
  LineAngle = 0
  LockPosition = false
  MeasureType = 1
  OverTolerance = 0
  References2D = -> [ProjItem]
  Rotation = 0
  ScaleType = 0
  TheoreticalExact = false
  Type = 6
  UnderTolerance = 0
  X = 36.3594
  Y = -100.059
FEATURE [TechDraw::DrawViewDimension] Dimension028
  AngleOverride = false
  Arbitrary = false
  ArbitraryTolerances = false
  EqualTolerance = true
  ExtensionAngle = 0
  FormatSpec = %.2w
  FormatSpecOverTolerance = %+.2w
  FormatSpecUnderTolerance = %+.2w
  Inverted = false
  LineAngle = 0
  LockPosition = false
  MeasureType = 1
  OverTolerance = 0
  References2D = -> [ProjItem]
  Rotation = 0
  ScaleType = 0
  TheoreticalExact = false
  Type = 0
  UnderTolerance = 0
  X = 70.3281
  Y = -74.709
FEATURE [TechDraw::DrawViewDimension] Dimension029
  AngleOverride = false
  Arbitrary = false
  ArbitraryTolerances = false
  EqualTolerance = true
  ExtensionAngle = 0
  FormatSpec = %.2w
  FormatSpecOverTolerance = %+.2w
  FormatSpecUnderTolerance = %+.2w
  Inverted = false
  LineAngle = 0
  LockPosition = false
  MeasureType = 1
  OverTolerance = 0
  References2D = -> [ProjItem]
  Rotation = 0
  ScaleType = 0
  TheoreticalExact = false
  Type = 0
  UnderTolerance = 0
  X = 61.9338
  Y = -67.1896
FEATURE [TechDraw::DrawViewDimension] Dimension030
  AngleOverride = false
  Arbitrary = false
  ArbitraryTolerances = false
  EqualTolerance = true
  ExtensionAngle = 0
  FormatSpec = %.2w
  FormatSpecOverTolerance = %+.2w
  FormatSpecUnderTolerance = %+.2w
  Inverted = false
  LineAngle = 0
  LockPosition = false
  MeasureType = 1
  OverTolerance = 0
  References2D = -> [ProjItem]
  Rotation = 0
  ScaleType = 0
  TheoreticalExact = false
  Type = 0
  UnderTolerance = 0
  X = 88.7714
  Y = -63.4181
FEATURE [TechDraw::DrawViewDimension] Dimension031
  AngleOverride = false
  Arbitrary = false
  ArbitraryTolerances = false
  EqualTolerance = true
  ExtensionAngle = 0
  FormatSpec = R%.2w
  FormatSpecOverTolerance = %+.2w
  FormatSpecUnderTolerance = %+.2w
  Inverted = false
  LineAngle = 0
  LockPosition = false
  MeasureType = 1
  OverTolerance = 0
  References2D = -> [ProjItem]
  Rotation = 0
  ScaleType = 0
  TheoreticalExact = false
  Type = 4
  UnderTolerance = 0
  X = 73.2825
  Y = -37.7687
FEATURE [TechDraw::DrawSVGTemplate] Template001
  Height = 297
  Orientation = 0
  Width = 210
FEATURE [TechDraw::DrawPage] Page001
  KeepUpdated = true
  NextBalloonIndex = 1
  ProjectionType = 0
  Template = -> Template001
FEATURE [TechDraw::DrawViewDimension] Dimension032
  AngleOverride = false
  Arbitrary = false
  ArbitraryTolerances = false
  EqualTolerance = true
  ExtensionAngle = 0
  FormatSpec = %.2w
  FormatSpecOverTolerance = %+.2w
  FormatSpecUnderTolerance = %+.2w
  Inverted = false
  LineAngle = 0
  LockPosition = false
  MeasureType = 1
  OverTolerance = 0
  References2D = -> [ProjItem]
  Rotation = 0
  ScaleType = 0
  TheoreticalExact = false
  Type = 0
  UnderTolerance = 0
  X = 11.0928
  Y = 9.31852
FEATURE [TechDraw::DrawViewDimension] Dimension033
  AngleOverride = false
  Arbitrary = false
  ArbitraryTolerances = false
  EqualTolerance = true
  ExtensionAngle = 0
  FormatSpec = %.2w
  FormatSpecOverTolerance = %+.2w
  FormatSpecUnderTolerance = %+.2w
  Inverted = false
  LineAngle = 0
  LockPosition = false
  MeasureType = 1
  OverTolerance = 0
  References2D = -> [ProjItem]
  Rotation = 0
  ScaleType = 0
  TheoreticalExact = false
  Type = 0
  UnderTolerance = 0
  X = -23.874
  Y = 22.5926
FEATURE [TechDraw::DrawViewDimension] Dimension034
  AngleOverride = false
  Arbitrary = false
  ArbitraryTolerances = false
  EqualTolerance = true
  ExtensionAngle = 0
  FormatSpec = %.2w
  FormatSpecOverTolerance = %+.2w
  FormatSpecUnderTolerance = %+.2w
  Inverted = false
  LineAngle = 0
  LockPosition = false
  MeasureType = 1
  OverTolerance = 0
  References2D = -> [ProjItem]
  Rotation = 0
  ScaleType = 0
  TheoreticalExact = false
  Type = 0
  UnderTolerance = 0
  X = -0.214661
  Y = 9.25545
FEATURE [TechDraw::DrawViewDimension] Dimension035
  AngleOverride = false
  Arbitrary = false
  ArbitraryTolerances = false
  EqualTolerance = true
  ExtensionAngle = 0
  FormatSpec = %.2w
  FormatSpecOverTolerance = %+.2w
  FormatSpecUnderTolerance = %+.2w
  Inverted = false
  LineAngle = 0
  LockPosition = false
  MeasureType = 1
  OverTolerance = 0
  References2D = -> [ProjItem]
  Rotation = 0
  ScaleType = 0
  TheoreticalExact = false
  Type = 0
  UnderTolerance = 0
  X = -11.1005
  Y = 28.3754
FEATURE [TechDraw::DrawViewDimension] Dimension036
  AngleOverride = false
  Arbitrary = false
  ArbitraryTolerances = false
  EqualTolerance = true
  ExtensionAngle = 0
  FormatSpec = %.2w
  FormatSpecOverTolerance = %+.2w
  FormatSpecUnderTolerance = %+.2w
  Inverted = false
  LineAngle = 0
  LockPosition = false
  MeasureType = 1
  OverTolerance = 0
  References2D = -> [ProjItem]
  Rotation = 0
  ScaleType = 0
  TheoreticalExact = false
  Type = 0
  UnderTolerance = 0
  X = 12.6534
  Y = 17.8523
FEATURE [TechDraw::DrawPage] Page
  KeepUpdated = true
  NextBalloonIndex = 1
  ProjectionType = 0
  Template = -> Template
  Views = -> [ProjGroup,Dimension,Dimension001,Dimension002,Dimension003,Dimension004,Dimension005,Dimension006,Dimension008,Dimension009,Dimension010,Dimension011,Dimension012,Dimension013,Dimension014,Dimension015,Dimension016,Dimension017,Dimension018,Dimension019,Dimension020,Dimension021,Dimension022,Dimension023,Dimension024,Dimension025,Dimension026,Dimension027,Dimension028,Dimension029,Dimension030,+6 more]
